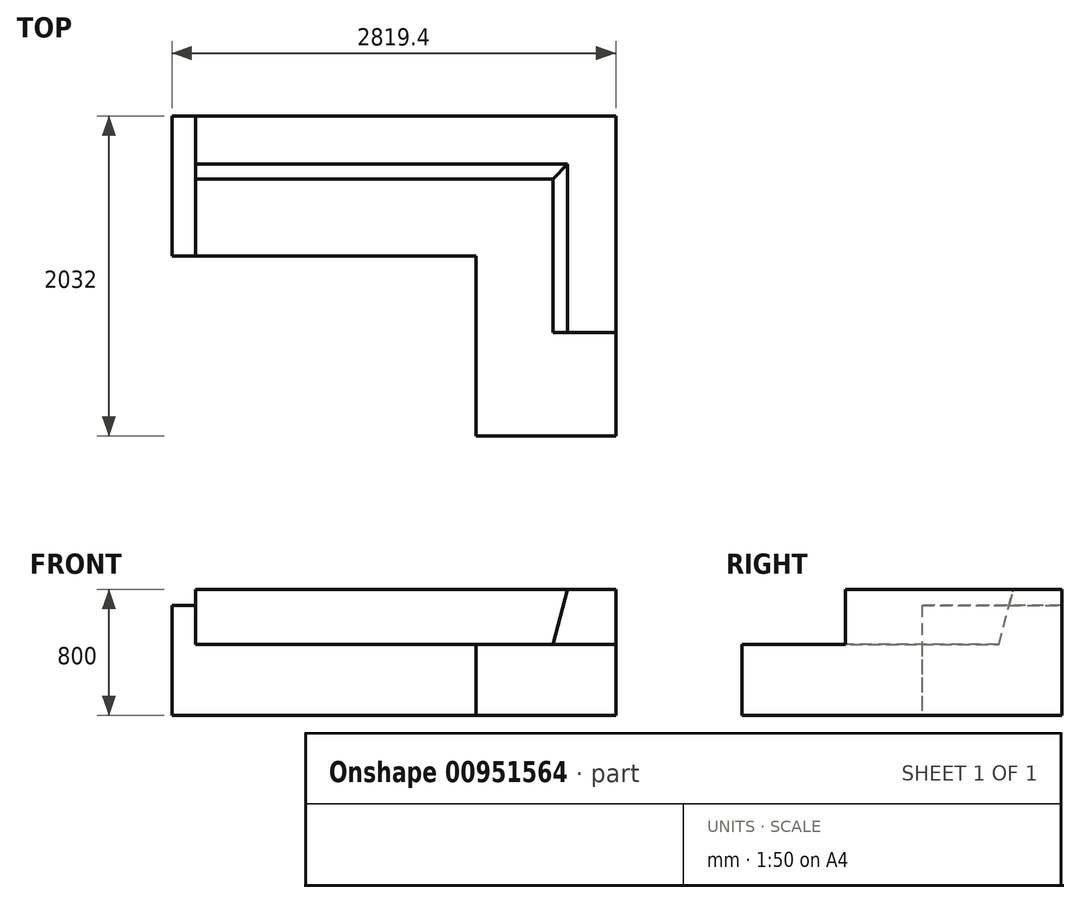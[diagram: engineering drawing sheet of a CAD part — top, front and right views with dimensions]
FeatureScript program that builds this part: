
annotation { "Feature Type Name" : "Feature", "Feature Type Description" : "" }
export const myFeature = defineFeature(function(context is Context, id is Id, definition is map)
    precondition{}
    {
        {
            var Q0;
            Q0=qCreatedBy(makeId("Top.planeOp"),FACE);
            var sketch = newSketch(context, id + "F0", { "sketchPlane" : qUnion([Q0])});
            skLineSegment(sketch, "E0", {"start": v(0, 0) * mm, "end": v(0, 2032) * mm});
            skLineSegment(sketch, "E1", {"start": v(0, 2032) * mm, "end": v(2819.4, 2032) * mm});
            skLineSegment(sketch, "E2", {"start": v(0, 0) * mm, "end": v(889, 0) * mm});
            skLineSegment(sketch, "E3", {"start": v(2819.4, 2032) * mm, "end": v(2819.4, 1143) * mm});
            skLineSegment(sketch, "E4", {"start": v(889, 0) * mm, "end": v(889, 1143) * mm});
            skLineSegment(sketch, "E5", {"start": v(889, 1143) * mm, "end": v(2819.4, 1143) * mm});
            skSolve(sketch);
        }
        {
            var Q0;
            Q0=qSketchRegion(id+"F0",true);
            extrude(context, id + "F1", {"entities" : qUnion([Q0]), "depth" : 450 * mm, "offsetDistance" : 25.4 * mm});
        }
        {
            var Q0;
            Q0=makeQuery(id+"F1.opExtrude","CAP_FACE",FACE,{"disambiguationData":[OSD([sQuery(id+"F0.wireOp",EDGE,"E0"),sQuery(id+"F0.wireOp",EDGE,"E1"),sQuery(id+"F0.wireOp",EDGE,"E2"),sQuery(id+"F0.wireOp",EDGE,"E3"),sQuery(id+"F0.wireOp",EDGE,"E4"),sQuery(id+"F0.wireOp",EDGE,"E5")])],"isStart":false});
            var sketch = newSketch(context, id + "F2", { "sketchPlane" : qUnion([Q0])});
            skLineSegment(sketch, "E6.bottom", {"start": v(889, 0) * mm, "end": v(0, 0) * mm});
            skLineSegment(sketch, "E6.top", {"start": v(889, 150) * mm, "end": v(0, 150) * mm});
            skLineSegment(sketch, "E6.left", {"start": v(889, 0) * mm, "end": v(889, 150) * mm});
            skLineSegment(sketch, "E6.right", {"start": v(0, 0) * mm, "end": v(0, 150) * mm});
            skLineSegment(sketch, "E7.bottom", {"start": v(2819.4, 1143) * mm, "end": v(2669.4, 1143) * mm});
            skLineSegment(sketch, "E7.top", {"start": v(2819.4, 2032) * mm, "end": v(2669.4, 2032) * mm});
            skLineSegment(sketch, "E7.left", {"start": v(2819.4, 1143) * mm, "end": v(2819.4, 2032) * mm});
            skLineSegment(sketch, "E7.right", {"start": v(2669.4, 1143) * mm, "end": v(2669.4, 2032) * mm});
            skSolve(sketch);
        }
        {
            var Q0;
            Q0=qSketchRegion(id+"F2",true);
            extrude(context, id + "F3", {"entities" : qUnion([Q0]), "operationType" : NewBodyOperationType.ADD, "depth" : 700 * mm - 450 * mm, "offsetDistance" : 25.4 * mm});
        }
        {
            var Q0;
            Q0=makeQuery(id+"F3.opExtrude","SWEPT_FACE",FACE,{"disambiguationData":[OSD([sQuery(id+"F2.wireOp",EDGE,"E6.top")])]});
            var sketch = newSketch(context, id + "F4", { "sketchPlane" : qUnion([Q0])});
            skLineSegment(sketch, "E8", {"start": v(0, 450) * mm, "end": v(0, 800) * mm});
            skLineSegment(sketch, "E9", {"start": v(0, 800) * mm, "end": v(-306.27, 800) * mm});
            skLineSegment(sketch, "E10", {"start": v(-306.27, 800) * mm, "end": v(-400.05, 450) * mm});
            skLineSegment(sketch, "E11", {"start": v(-400.05, 450) * mm, "end": v(0, 450) * mm});
            skSolve(sketch);
        }
        {
            var Q0;
            Q0=qSketchRegion(id+"F4",true);
            var Q1;
            Q1=makeQuery(id+"F3.boolean.opBoolean","MERGE",FACE,{"derivedFrom":[makeQuery(id+"F1.opExtrude","SWEPT_FACE",FACE,{"disambiguationData":[OSD([sQuery(id+"F0.wireOp",EDGE,"E1")])]}),makeQuery(id+"F3.opExtrude","SWEPT_FACE",FACE,{"disambiguationData":[OSD([sQuery(id+"F2.wireOp",EDGE,"E7.top")])]})]});
            extrude(context, id + "F5", {"entities" : qUnion([Q0]), "operationType" : NewBodyOperationType.ADD, "endBound" : BoundingType.UP_TO_SURFACE, "depth" : 25.4 * mm, "endBoundEntityFace" : qUnion([Q1]), "offsetDistance" : 25.4 * mm});
        }
        {
            var Q0;
            Q0=makeQuery(id+"F3.opExtrude","SWEPT_FACE",FACE,{"disambiguationData":[OSD([sQuery(id+"F2.wireOp",EDGE,"E7.right")])]});
            var sketch = newSketch(context, id + "F6", { "sketchPlane" : qUnion([Q0])});
            skLineSegment(sketch, "E12", {"start": v(-2032, 450) * mm, "end": v(-1631.95, 450) * mm});
            skLineSegment(sketch, "E13", {"start": v(-1631.95, 450) * mm, "end": v(-1725.73, 800) * mm});
            skLineSegment(sketch, "E14", {"start": v(-1725.73, 800) * mm, "end": v(-2032, 800) * mm});
            skLineSegment(sketch, "E15", {"start": v(-2032, 800) * mm, "end": v(-2032, 450) * mm});
            skSolve(sketch);
        }
        {
            var Q0;
            Q0=qSketchRegion(id+"F6",true);
            extrude(context, id + "F7", {"entities" : qUnion([Q0]), "operationType" : NewBodyOperationType.ADD, "endBound" : BoundingType.UP_TO_NEXT, "depth" : 25.4 * mm, "offsetDistance" : 25.4 * mm});
        }
        {
            var Q0;
            Q0=makeQuery(id+"F3.boolean.opBoolean","MERGE",FACE,{"derivedFrom":[makeQuery(id+"F1.opExtrude","SWEPT_FACE",FACE,{"disambiguationData":[OSD([sQuery(id+"F0.wireOp",EDGE,"E4")])]}),makeQuery(id+"F3.opExtrude","SWEPT_FACE",FACE,{"disambiguationData":[OSD([sQuery(id+"F2.wireOp",EDGE,"E6.left")])]})]});
            var sketch = newSketch(context, id + "F8", { "sketchPlane" : qUnion([Q0])});
            skLineSegment(sketch, "E16.bottom", {"start": v(658.57, 450) * mm, "end": v(0, 450) * mm});
            skLineSegment(sketch, "E16.top", {"start": v(658.57, 800) * mm, "end": v(0, 800) * mm});
            skLineSegment(sketch, "E16.left", {"start": v(658.57, 450) * mm, "end": v(658.57, 800) * mm});
            skLineSegment(sketch, "E16.right", {"start": v(0, 450) * mm, "end": v(0, 800) * mm});
            skSolve(sketch);
        }
        {
            var Q0;
            Q0=qSketchRegion(id+"F8",true);
            extrude(context, id + "F9", {"entities" : qUnion([Q0]), "operationType" : NewBodyOperationType.REMOVE, "endBound" : BoundingType.THROUGH_ALL, "oppositeDirection" : true, "depth" : 25.4 * mm, "offsetDistance" : 25.4 * mm});
        }
        {
            var Q0;
            Q0=makeQuery(id+"F1.opExtrude","SWEPT_BODY",BODY,{"disambiguationData":[OSD([sQuery(id+"F0.wireOp",EDGE,"E0"),sQuery(id+"F0.wireOp",EDGE,"E1"),sQuery(id+"F0.wireOp",EDGE,"E2"),sQuery(id+"F0.wireOp",EDGE,"E3"),sQuery(id+"F0.wireOp",EDGE,"E4"),sQuery(id+"F0.wireOp",EDGE,"E5")])]});
            var Q1;
            Q1=qCreatedBy(makeId("Right.planeOp"),FACE);
            mirror(context, id + "F10", {"operationType" : NewBodyOperationType.ADD, "entities" : qUnion([Q0]), "mirrorPlane" : qUnion([Q1])});
        }
        {
            var Q0;
            Q0=qCreatedBy(makeId("Right.planeOp"),FACE);
            var sketch = newSketch(context, id + "F11", { "sketchPlane" : qUnion([Q0])});
            skLineSegment(sketch, "E17.bottom", {"start": v(-309.58, -291.68) * mm, "end": v(2775.67, -291.68) * mm});
            skLineSegment(sketch, "E17.top", {"start": v(-309.58, 953.1) * mm, "end": v(2775.67, 953.1) * mm});
            skLineSegment(sketch, "E17.left", {"start": v(-309.58, -291.68) * mm, "end": v(-309.58, 953.1) * mm});
            skLineSegment(sketch, "E17.right", {"start": v(2775.67, -291.68) * mm, "end": v(2775.67, 953.1) * mm});
            skSolve(sketch);
        }
        {
            var Q0;
            Q0=qSketchRegion(id+"F11",true);
            extrude(context, id + "F12", {"entities" : qUnion([Q0]), "operationType" : NewBodyOperationType.REMOVE, "endBound" : BoundingType.THROUGH_ALL, "depth" : 25.4 * mm, "offsetDistance" : 25.4 * mm});
        }
    });
